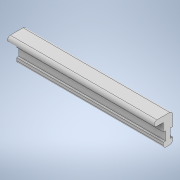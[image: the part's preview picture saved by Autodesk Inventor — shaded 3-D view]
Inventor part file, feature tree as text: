
AUTODESK INVENTOR PART (.ipt)
format: ipt  version: 2020 (Build 240168000, 168)  size: 140,800 bytes
history: native  units: in
note: dims shown in document units (in); Inventor stores cm internally (conversion verified against a paired STEP export)
features: extrude x3, sketch x3, fillet x2
ambient origin geometry x8: Origin, YZ Plane, XZ Plane, XY Plane, X Axis, Y Axis, Z Axis, Center Point
bodies: Solid1 (feature_tree)
feature tree (8):
  extrude  "Extrusion1"  Depth=3.1496in
  extrude  "Extrusion2"  Depth=0.1043in
  extrude  "Extrusion3"  Depth=0.2953in
  fillet  "Fillet1"  Radius=0.1181in
  fillet  "Fillet2"  Radius=0.1969in
  sketch  "Sketch1"  dims[d0=0.1969in d1=3.1496in]
  sketch  "Sketch2"  dims[d2=0.1181in d3=0.0in d4=0.1043in]
  sketch  "Sketch3"  dims[d5=0.19in d6=0.0in d7=0.2953in d8=0.1181in d9=0.1969in d10=0.19in d11=0.0in d12=0.0591in d13=0.0591in]
